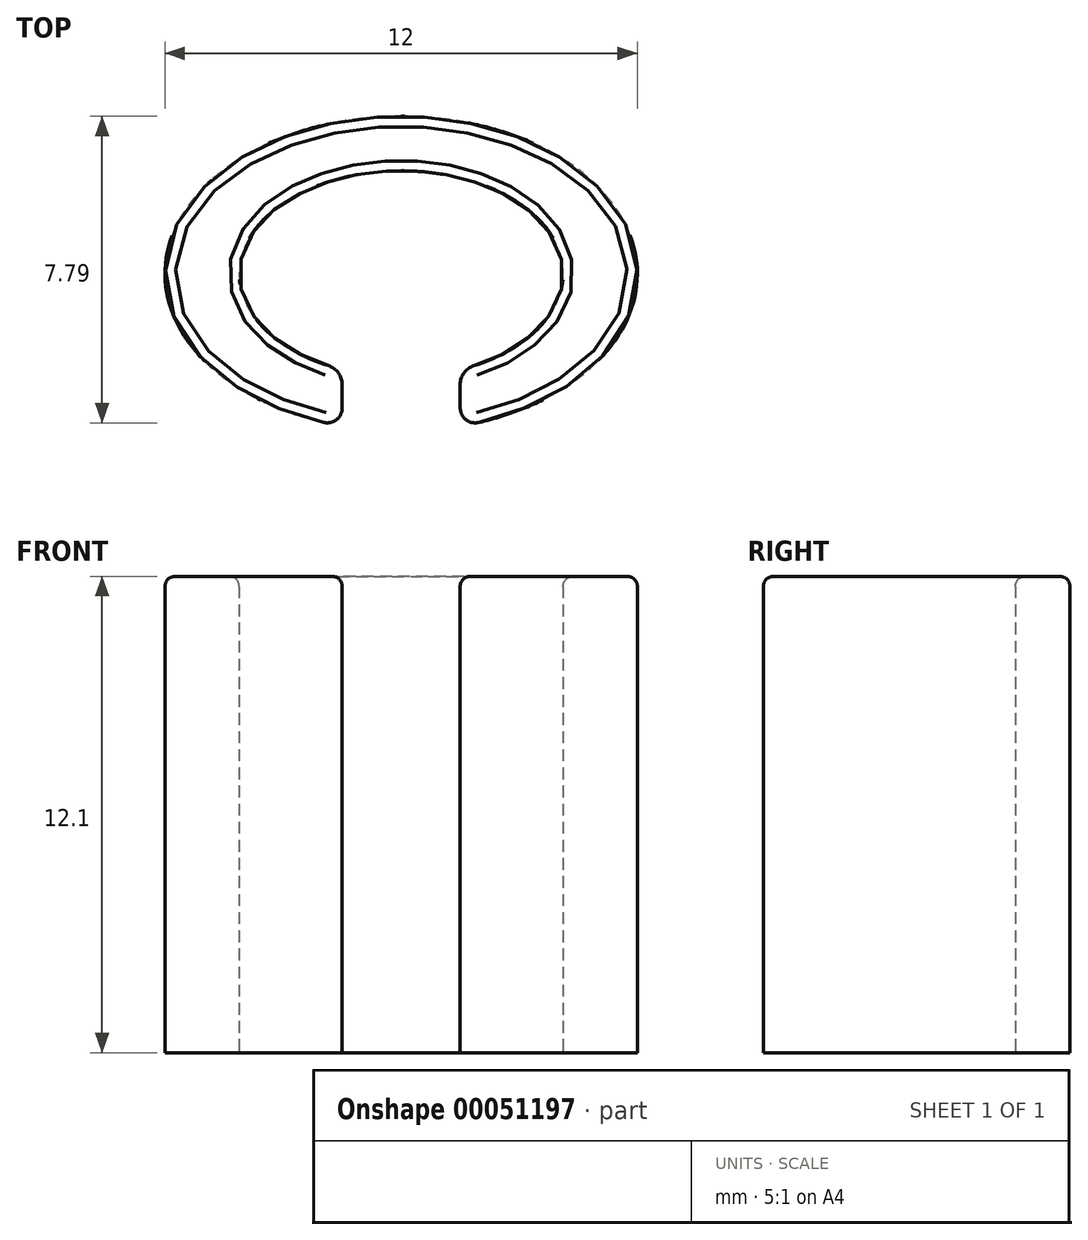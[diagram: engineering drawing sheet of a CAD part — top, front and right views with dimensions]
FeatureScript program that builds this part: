
annotation { "Feature Type Name" : "Feature", "Feature Type Description" : "" }
export const myFeature = defineFeature(function(context is Context, id is Id, definition is map)
    precondition{}
    {
        {
            var Q0;
            Q0=qCreatedBy(makeId("Top.planeOp"),FACE);
            var sketch = newSketch(context, id + "F0", { "sketchPlane" : qUnion([Q0])});
            skEllipse(sketch, "E0", {"center": v(0, 0) * mm, "majorRadius": 4.12 * mm, "minorRadius": 2.62 * mm, "majorAxis": v(1, 0)});
            skEllipse(sketch, "E1", {"center": v(0, 0) * mm, "majorRadius": 6 * mm, "minorRadius": 4 * mm, "majorAxis": v(1, 0)});
            skSolve(sketch);
        }
        {
            var Q0;
            Q0=qCreatedBy(makeId("Top.planeOp"),FACE);
            var sketch = newSketch(context, id + "F1", { "sketchPlane" : qUnion([Q0])});
            skEllipse(sketch, "E2", {"center": v(0, 0) * mm, "majorRadius": 5.3 * mm, "minorRadius": 3.8 * mm, "majorAxis": v(1, 0)});
            skSolve(sketch);
        }
        {
            var Q0;
            Q0=makeQuery(id+"F0.imprint","IMPRINT",FACE,{"disambiguationData":[TD([[makeQuery(id+"F0.imprint","IMPRINT",EDGE,{"derivedFrom":sQuery(id+"F0.wireOp",EDGE,"E0")}),-1.0]])]});
            extrude(context, id + "F2", {"entities" : qUnion([Q0]), "depth" : 12.1 * mm});
        }
        {
            var Q0;
            Q0=qCreatedBy(makeId("Top.planeOp"),FACE);
            var sketch = newSketch(context, id + "F3", { "sketchPlane" : qUnion([Q0])});
            skLineSegment(sketch, "E3", {"start": v(-1.5, 0) * mm, "end": v(1.5, 0) * mm});
            skLineSegment(sketch, "E4.top", {"start": v(-1.5, -7.88) * mm, "end": v(1.5, -7.88) * mm});
            skLineSegment(sketch, "E4.left", {"start": v(-1.5, 0) * mm, "end": v(-1.5, -7.88) * mm});
            skLineSegment(sketch, "E4.right", {"start": v(1.5, 0) * mm, "end": v(1.5, -7.88) * mm});
            skSolve(sketch);
        }
        {
            var Q0;
            Q0=makeQuery(id+"F3.imprint","IMPRINT",FACE,{"disambiguationData":[TD([[makeQuery(id+"F3.imprint","IMPRINT",EDGE,{"derivedFrom":sQuery(id+"F3.wireOp",EDGE,"E3")}),-1.0]])]});
            extrude(context, id + "F4", {"entities" : qUnion([Q0]), "operationType" : NewBodyOperationType.REMOVE, "depth" : 25.4 * mm});
        }
        {
            var Q0;
            {var subQ0=sQuery(id+"F0.wireOp",EDGE,"E0");var subQ1=makeQuery(id+"F4.opExtrude","SWEPT_FACE",FACE,{"disambiguationData":[OSD([sQuery(id+"F3.wireOp",EDGE,"E4.right")])]});var subQ2=makeQuery(id+"F2.opExtrude","SWEPT_FACE",FACE,{"disambiguationData":[OSD([subQ0])]});Q0=makeQuery(id+"FYo5K6hidE1Kwi3_1.boolean.opBoolean","SPLIT",EDGE,{"disambiguationData":[TD([makeQuery(id+"F2.opExtrude","CAP_FACE",FACE,{"disambiguationData":[OSD([subQ0,sQuery(id+"F0.wireOp",EDGE,"E1")])],"isStart":false})])],"derivedFrom":makeQuery(id+"F4.boolean.opBoolean","INTERSECT",EDGE,{"derivedFrom":[subQ2,subQ1]})});}
            var Q1;
            {var subQ0=sQuery(id+"F0.wireOp",EDGE,"E0");var subQ1=makeQuery(id+"F4.opExtrude","SWEPT_FACE",FACE,{"disambiguationData":[OSD([sQuery(id+"F3.wireOp",EDGE,"E4.left")])]});var subQ2=makeQuery(id+"F2.opExtrude","SWEPT_FACE",FACE,{"disambiguationData":[OSD([subQ0])]});Q1=makeQuery(id+"FYo5K6hidE1Kwi3_1.boolean.opBoolean","SPLIT",EDGE,{"disambiguationData":[TD([makeQuery(id+"F2.opExtrude","CAP_FACE",FACE,{"disambiguationData":[OSD([subQ0,sQuery(id+"F0.wireOp",EDGE,"E1")])],"isStart":false})])],"derivedFrom":makeQuery(id+"F4.boolean.opBoolean","INTERSECT",EDGE,{"derivedFrom":[subQ2,subQ1]})});}
            fillet(context, id + "F5", {"entities" : qUnion([Q0, Q1]), "radius" : 0.5 * mm, "tangentPropagation" : true, "allowEdgeOverflow" : false});
        }
        {
            var Q0;
            Q0=makeQuery(id+"F4.boolean.opBoolean","INTERSECT",EDGE,{"derivedFrom":[makeQuery(id+"F2.opExtrude","SWEPT_FACE",FACE,{"disambiguationData":[OSD([sQuery(id+"F0.wireOp",EDGE,"E1")])]}),makeQuery(id+"F4.opExtrude","SWEPT_FACE",FACE,{"disambiguationData":[OSD([sQuery(id+"F3.wireOp",EDGE,"E4.right")])]})]});
            var Q1;
            Q1=makeQuery(id+"F4.boolean.opBoolean","INTERSECT",EDGE,{"derivedFrom":[makeQuery(id+"F2.opExtrude","SWEPT_FACE",FACE,{"disambiguationData":[OSD([sQuery(id+"F0.wireOp",EDGE,"E1")])]}),makeQuery(id+"F4.opExtrude","SWEPT_FACE",FACE,{"disambiguationData":[OSD([sQuery(id+"F3.wireOp",EDGE,"E4.left")])]})]});
            fillet(context, id + "F6", {"entities" : qUnion([Q0, Q1]), "radius" : 0.38 * mm, "tangentPropagation" : true, "allowEdgeOverflow" : false});
        }
        {
            var Q0;
            Q0=makeQuery(id+"F2.opExtrude","CAP_EDGE",EDGE,{"disambiguationData":[OSD([sQuery(id+"F0.wireOp",EDGE,"E0")])],"isStart":false});
            var Q1;
            Q1=makeQuery(id+"F2.opExtrude","CAP_EDGE",EDGE,{"disambiguationData":[OSD([sQuery(id+"F0.wireOp",EDGE,"E1")])],"isStart":false});
            var Q2;
            {var subQ0=sQuery(id+"F0.wireOp",EDGE,"E0");Q2=makeQuery(id+"F5.opFillet","BLEND_EDGE",EDGE,{"blendedFrom":[makeQuery(id+"F4.boolean.opBoolean","INTERSECT",EDGE,{"derivedFrom":[makeQuery(id+"F2.opExtrude","SWEPT_FACE",FACE,{"disambiguationData":[OSD([subQ0])]}),makeQuery(id+"F4.opExtrude","SWEPT_FACE",FACE,{"disambiguationData":[OSD([sQuery(id+"F3.wireOp",EDGE,"E4.left")])]})]}),makeQuery(id+"F2.opExtrude","CAP_FACE",FACE,{"disambiguationData":[OSD([subQ0,sQuery(id+"F0.wireOp",EDGE,"E1")])],"isStart":false})],"blendedInto":[makeQuery(id+"F2.opExtrude","CAP_FACE",FACE,{"disambiguationData":[OSD([subQ0,sQuery(id+"F0.wireOp",EDGE,"E1")])],"isStart":false})]});}
            var Q3;
            Q3=makeQuery(id+"F4.boolean.opBoolean","INTERSECT",EDGE,{"derivedFrom":[makeQuery(id+"F2.opExtrude","CAP_FACE",FACE,{"disambiguationData":[OSD([sQuery(id+"F0.wireOp",EDGE,"E0"),sQuery(id+"F0.wireOp",EDGE,"E1")])],"isStart":false}),makeQuery(id+"F4.opExtrude","SWEPT_FACE",FACE,{"disambiguationData":[OSD([sQuery(id+"F3.wireOp",EDGE,"E4.left")])]})]});
            var Q4;
            {var subQ0=sQuery(id+"F0.wireOp",EDGE,"E1");Q4=makeQuery(id+"F6.opFillet","BLEND_EDGE",EDGE,{"blendedFrom":[makeQuery(id+"F4.boolean.opBoolean","INTERSECT",EDGE,{"derivedFrom":[makeQuery(id+"F2.opExtrude","SWEPT_FACE",FACE,{"disambiguationData":[OSD([subQ0])]}),makeQuery(id+"F4.opExtrude","SWEPT_FACE",FACE,{"disambiguationData":[OSD([sQuery(id+"F3.wireOp",EDGE,"E4.left")])]})]}),makeQuery(id+"F2.opExtrude","CAP_FACE",FACE,{"disambiguationData":[OSD([sQuery(id+"F0.wireOp",EDGE,"E0"),subQ0])],"isStart":false})],"blendedInto":[makeQuery(id+"F2.opExtrude","CAP_FACE",FACE,{"disambiguationData":[OSD([sQuery(id+"F0.wireOp",EDGE,"E0"),subQ0])],"isStart":false})]});}
            var Q5;
            {var subQ0=sQuery(id+"F0.wireOp",EDGE,"E1");Q5=makeQuery(id+"F6.opFillet","BLEND_EDGE",EDGE,{"blendedFrom":[makeQuery(id+"F4.boolean.opBoolean","INTERSECT",EDGE,{"derivedFrom":[makeQuery(id+"F2.opExtrude","SWEPT_FACE",FACE,{"disambiguationData":[OSD([subQ0])]}),makeQuery(id+"F4.opExtrude","SWEPT_FACE",FACE,{"disambiguationData":[OSD([sQuery(id+"F3.wireOp",EDGE,"E4.right")])]})]}),makeQuery(id+"F2.opExtrude","CAP_FACE",FACE,{"disambiguationData":[OSD([sQuery(id+"F0.wireOp",EDGE,"E0"),subQ0])],"isStart":false})],"blendedInto":[makeQuery(id+"F2.opExtrude","CAP_FACE",FACE,{"disambiguationData":[OSD([sQuery(id+"F0.wireOp",EDGE,"E0"),subQ0])],"isStart":false})]});}
            var Q6;
            Q6=makeQuery(id+"F4.boolean.opBoolean","INTERSECT",EDGE,{"derivedFrom":[makeQuery(id+"F2.opExtrude","CAP_FACE",FACE,{"disambiguationData":[OSD([sQuery(id+"F0.wireOp",EDGE,"E0"),sQuery(id+"F0.wireOp",EDGE,"E1")])],"isStart":false}),makeQuery(id+"F4.opExtrude","SWEPT_FACE",FACE,{"disambiguationData":[OSD([sQuery(id+"F3.wireOp",EDGE,"E4.right")])]})]});
            var Q7;
            {var subQ0=sQuery(id+"F0.wireOp",EDGE,"E0");Q7=makeQuery(id+"F5.opFillet","BLEND_EDGE",EDGE,{"blendedFrom":[makeQuery(id+"F4.boolean.opBoolean","INTERSECT",EDGE,{"derivedFrom":[makeQuery(id+"F2.opExtrude","SWEPT_FACE",FACE,{"disambiguationData":[OSD([subQ0])]}),makeQuery(id+"F4.opExtrude","SWEPT_FACE",FACE,{"disambiguationData":[OSD([sQuery(id+"F3.wireOp",EDGE,"E4.right")])]})]}),makeQuery(id+"F2.opExtrude","CAP_FACE",FACE,{"disambiguationData":[OSD([subQ0,sQuery(id+"F0.wireOp",EDGE,"E1")])],"isStart":false})],"blendedInto":[makeQuery(id+"F2.opExtrude","CAP_FACE",FACE,{"disambiguationData":[OSD([subQ0,sQuery(id+"F0.wireOp",EDGE,"E1")])],"isStart":false})]});}
            fillet(context, id + "F7", {"entities" : qUnion([Q0, Q1, Q2, Q3, Q4, Q5, Q6, Q7]), "radius" : 0.25 * mm, "tangentPropagation" : true, "allowEdgeOverflow" : false});
        }
    });
